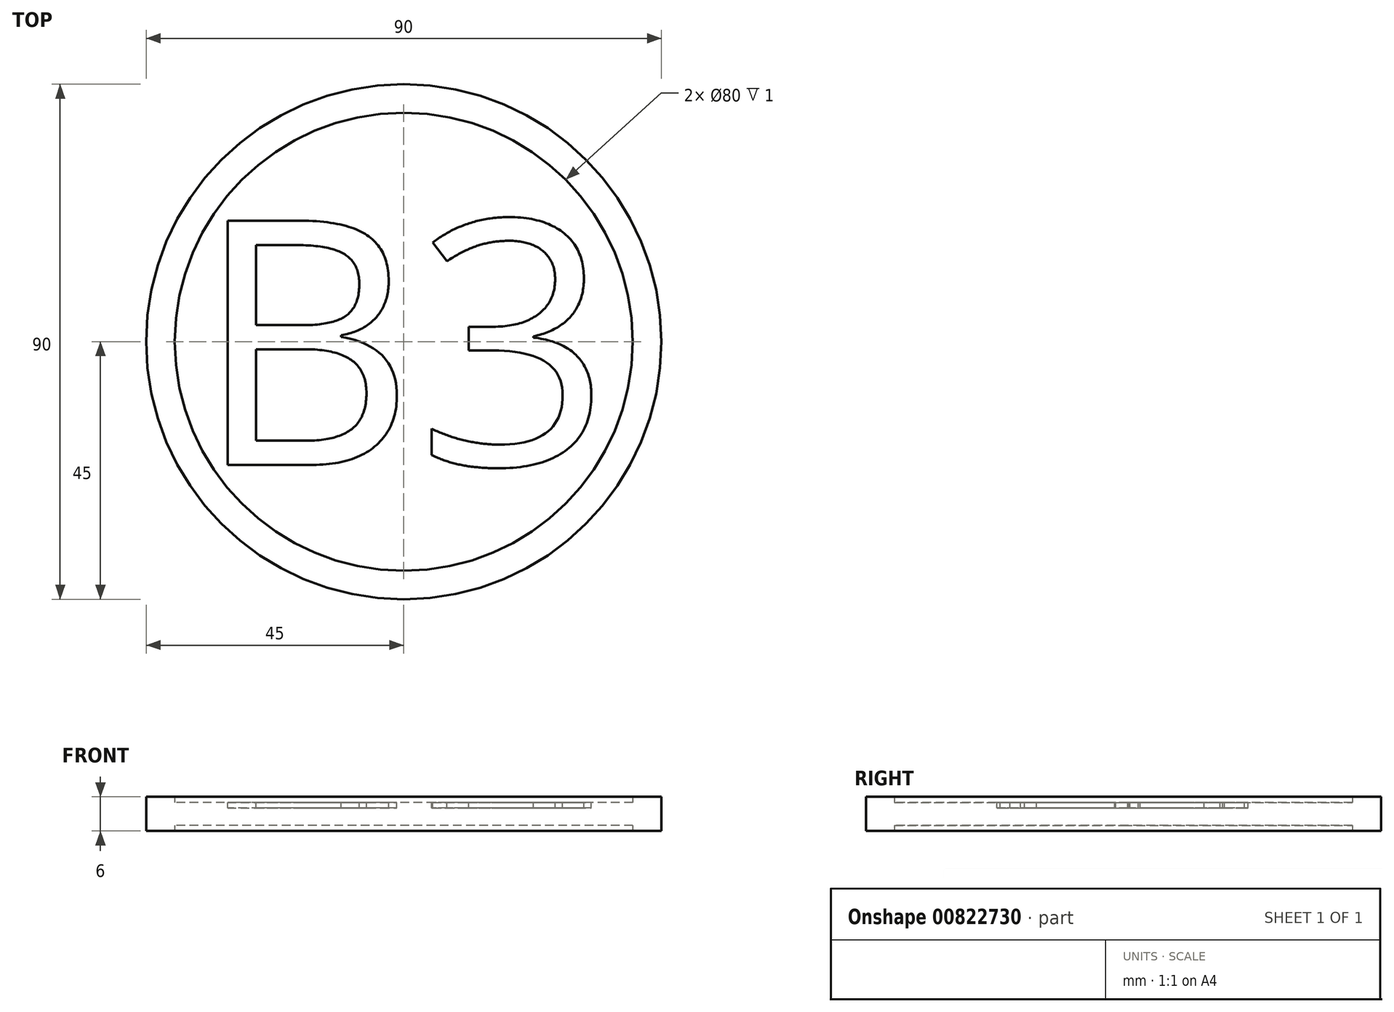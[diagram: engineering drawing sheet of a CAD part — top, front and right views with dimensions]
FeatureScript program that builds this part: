
annotation { "Feature Type Name" : "Feature", "Feature Type Description" : "" }
export const myFeature = defineFeature(function(context is Context, id is Id, definition is map)
    precondition{}
    {
        {
            var Q0;
            Q0=qCreatedBy(makeId("Top.planeOp"),FACE);
            var sketch = newSketch(context, id + "F0", { "sketchPlane" : qUnion([Q0])});
            skCircle(sketch, "E0", {"center": v(0, 0) * mm, "radius": 40 * mm});
            skCircle(sketch, "E1.0", {"center": v(0, 0) * mm, "radius": 45 * mm});
            skSolve(sketch);
        }
        {
            var Q0;
            Q0=makeQuery(id+"F0.imprint","IMPRINT",FACE,{"disambiguationData":[TD([[makeQuery(id+"F0.imprint","IMPRINT",EDGE,{"derivedFrom":sQuery(id+"F0.wireOp",EDGE,"E0")}),1.0]])]});
            extrude(context, id + "F1", {"entities" : qUnion([Q0]), "depth" : 2 * mm, "offsetDistance" : 25 * mm, "hasSecondDirection" : true, "secondDirectionOppositeDirection" : true, "secondDirectionDepth" : 2 * mm});
        }
        {
            var Q0;
            Q0=makeQuery(id+"F0.imprint","IMPRINT",FACE,{"disambiguationData":[TD([[makeQuery(id+"F0.imprint","IMPRINT",EDGE,{"derivedFrom":sQuery(id+"F0.wireOp",EDGE,"E0")}),-1.0]])]});
            extrude(context, id + "F2", {"entities" : qUnion([Q0]), "operationType" : NewBodyOperationType.ADD, "depth" : 3 * mm, "offsetDistance" : 25 * mm, "hasSecondDirection" : true, "secondDirectionOppositeDirection" : true, "secondDirectionDepth" : 3 * mm});
        }
        {
            var Q0;
            Q0=makeQuery(id+"F1.opExtrude","CAP_FACE",FACE,{"disambiguationData":[OSD([sQuery(id+"F0.wireOp",EDGE,"E0")])],"isStart":false});
            var sketch = newSketch(context, id + "F3", { "sketchPlane" : qUnion([Q0])});
            skText(sketch, "E2", { "text": "B3", "fontName": "OpenSans-Regular.ttf"});
            skLineSegment(sketch, "E3", {"start": v(-36.65, 21.52) * mm, "end": v(36.65, -21.52) * mm, "construction": true});
            const initialGuessF3  = {"E2": [-0.03665, -0.02152, 1, 0, 0.04305]};
            skSetInitialGuess(sketch, initialGuessF3);
            skSolve(sketch);
        }
        {
            var Q0;
            Q0 = qSketchRegion(id + "F3", true);
            extrude(context, id + "F4", {"entities" : qUnion([Q0]), "operationType" : NewBodyOperationType.REMOVE, "oppositeDirection" : true, "depth" : 1 * mm, "offsetDistance" : 25 * mm});
        }
    });
